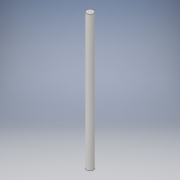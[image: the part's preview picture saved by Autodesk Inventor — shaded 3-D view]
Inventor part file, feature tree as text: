
AUTODESK INVENTOR PART (.ipt)
format: ipt  version: 2019 (Build 230136000, 136)  size: 89,088 bytes
history: native  units: in
note: dims shown in document units (in); Inventor stores cm internally (conversion verified against a paired STEP export)
features: extrude x1, sketch x1
ambient origin geometry x8: Origin, YZ Plane, XZ Plane, XY Plane, X Axis, Y Axis, Z Axis, Center Point
bodies: Solid1 (feature_tree)
feature tree (2):
  extrude  "Extrusion1"  Depth=11.811in TaperAngle=0.0deg
  sketch  "Sketch1"  dims[d0=0.5906in d1=11.811in d2=0.0in]
